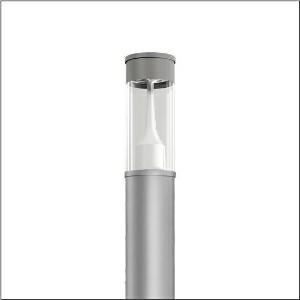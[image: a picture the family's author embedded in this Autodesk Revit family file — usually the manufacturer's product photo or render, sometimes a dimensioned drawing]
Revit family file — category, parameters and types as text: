
# Revit family: city-light_260_iq___pl1_2s_5xa5295of14h_8957
name_source: partatom
category: Lighting Fixtures
units: mm (PartAtom-declared; Revit-internal decimal feet)

## family parameters
Cut with Voids When Loaded = No
Host = Face
Light Source = No
Part Type = Normal
Room Calculation Point = No
Round Connector Dimension = Use Diameter
Shared = No

## types (1)
- --- (1 x LED, 2970 lm, 21.8 W, 2700K)
    Apparent Load = 22 VA
    CIE Flux Codes = 23 62 94 96 100
    Color Rendering = 70
    Color Temperature = 2700K
    Default Elevation = 1800 mm
    Description = City-Light 260 iQ, light pillar, Module 540 iQ-SR, primary light control with 3 zone facetted reflector, of plastic, silver coated, highly specular, structured, primary optical cover: cover, of PMMA, transparent, partly coated, light distribution: PL1.2s, primary light characteristic: symmetric, LED, High Power LED, rated luminous flux: 2.970lm, luminous efficacy: 136lm/W, light colour: 727, colour temperature: 2700K, control gear: iQ Street-Remote, control: pre-setting: logarithmic dimming characteristic, Street-Remote, Auto-Match, Temp-Guard, Lumen-Switch, Night-Set, Smart-Wire, Light-Fading, Desk-Remote (wireless, voltage-free reading and setting of iQ features in the workshop via application-optimized NFC function/RFID function), optimised constant luminous flux control (CLO 2.0), with terminal, 6-pole, max. 2.5mm², mains connection: 230..240V, AC, 50/60Hz, start of lifetime: 22W, end of service life: 23W, reduction: 11W, luminaire housing, cylindrical, of extruded aluminium section, coated, Siteco® metallic grey (DB 702S), length: 2.600mm, diameter: 200mm, Module 540 iQ-SR, traffic white (RAL 9016), equipment: standard, protection rating (complete): IP65, insulation class (complete): insulation class II (safety insulation), certification: CE, ENEC, VDE, packaging unit: 1 piece

Light Distribution: PL1.2s
    Height = 500 mm
    Lamp = 1 x LED
    Lamp Light Flux = 2970 lm
    Lamp Power = 21.8 W
    Lamp count = 1
    Length = 200 mm  [stored 0.656168 ft]
    Luminous efficacy = 136 lm/W
    Manufacturer = Siteco
    ModVariant = No
    Model = 5XA5295OF14H
    Mounting Place = Floor
    Mounting Type = Freestanding
    Number of Poles = 1
    OnlyDefault = Yes
    Power Factor = 1
    Product Name = City-Light 260 iQ | PL1.2s
    Product group = light pillar
    ProductGroupID = 1301
    Protection Class = Protection class II
    Protection Degree = IP 65
    RLX_Detail_Level = 1
    RLX_Emergency_Light_Flux = 0 lm
    RLX_Emergency_Type = 0
    RLX_Emergency_Type_DB = No
    RlxData = <blob elided: 28745 chars, md5=62fdd889>
    Socket = socket
    Standby Power = 0 W
    System Light Flux = 2970 lm
    System Power = 22 W
    Type Comments = factory setting: luminous flux: 100 % | dim-lin: 254 | 456 mA
    Type Image = l_1006920.jpg
    URL = http://relux.com
    VarID = @adj_144433
    Voltage = 0 V
    Weight = 0.00 kg
    Width = 0 mm  [stored 0 ft]

note: [stored X ft] marks values corroborated as IEEE doubles in the binary element streams (Revit-internal decimal feet)

## geometry (parser evidence)
native form markers: Blend x4, Sweep x11
no freeform markers — native parametric forms only
